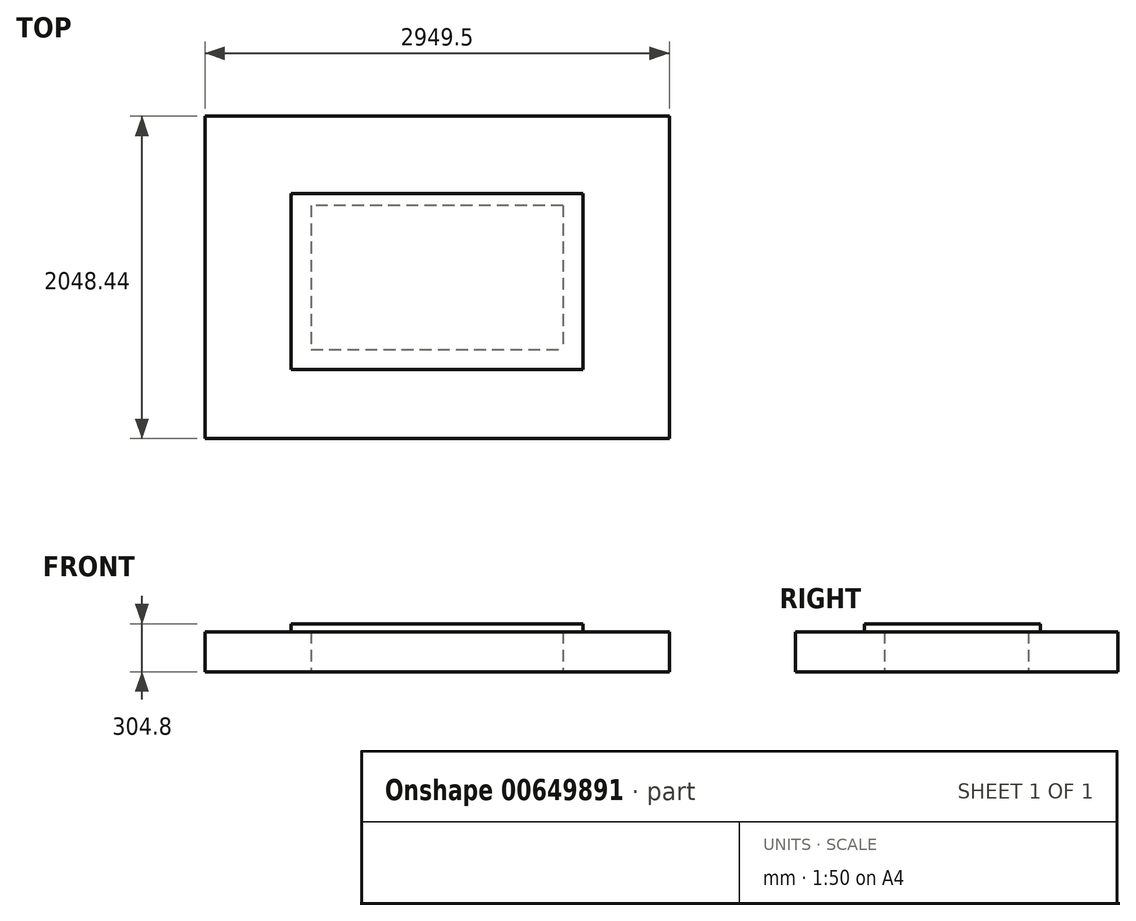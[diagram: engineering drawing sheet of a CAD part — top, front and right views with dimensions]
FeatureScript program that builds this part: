
annotation { "Feature Type Name" : "Feature", "Feature Type Description" : "" }
export const myFeature = defineFeature(function(context is Context, id is Id, definition is map)
    precondition{}
    {
        {
            var Q0;
            Q0=qCreatedBy(makeId("Top.planeOp"),FACE);
            var sketch = newSketch(context, id + "F0", { "sketchPlane" : qUnion([Q0])});
            skLineSegment(sketch, "E0.bottom", {"start": v(800.1, -457.2) * mm, "end": v(-800.1, -457.2) * mm});
            skLineSegment(sketch, "E0.top", {"start": v(800.1, 457.2) * mm, "end": v(-800.1, 457.2) * mm});
            skLineSegment(sketch, "E0.left", {"start": v(800.1, -457.2) * mm, "end": v(800.1, 457.2) * mm});
            skLineSegment(sketch, "E0.right", {"start": v(-800.1, -457.2) * mm, "end": v(-800.1, 457.2) * mm});
            skPoint(sketch, "E0.middle", {"position": v(0, 0) * mm});
            skLineSegment(sketch, "E1.bottom", {"start": v(1474.75, -1024.22) * mm, "end": v(-1474.75, -1024.22) * mm});
            skLineSegment(sketch, "E1.top", {"start": v(1474.75, 1024.22) * mm, "end": v(-1474.75, 1024.22) * mm});
            skLineSegment(sketch, "E1.left", {"start": v(1474.75, -1024.22) * mm, "end": v(1474.75, 1024.22) * mm});
            skLineSegment(sketch, "E1.right", {"start": v(-1474.75, -1024.22) * mm, "end": v(-1474.75, 1024.22) * mm});
            skSolve(sketch);
        }
        {
            var Q0;
            Q0=makeQuery(id+"F0.imprint","IMPRINT",FACE,{"disambiguationData":[TD([[makeQuery(id+"F0.imprint","IMPRINT",EDGE,{"derivedFrom":sQuery(id+"F0.wireOp",EDGE,"E0.bottom")}),1.0]])]});
            extrude(context, id + "F1", {"entities" : qUnion([Q0]), "depth" : 254 * mm, "offsetDistance" : 25.4 * mm});
        }
        {
            var Q0;
            Q0=makeQuery(id+"F1.opExtrude","CAP_FACE",FACE,{"disambiguationData":[OSD([sQuery(id+"F0.wireOp",EDGE,"E0.bottom"),sQuery(id+"F0.wireOp",EDGE,"E0.top"),sQuery(id+"F0.wireOp",EDGE,"E0.left"),sQuery(id+"F0.wireOp",EDGE,"E0.right"),sQuery(id+"F0.wireOp",EDGE,"E1.bottom"),sQuery(id+"F0.wireOp",EDGE,"E1.top"),sQuery(id+"F0.wireOp",EDGE,"E1.left"),sQuery(id+"F0.wireOp",EDGE,"E1.right")])],"isStart":false});
            var sketch = newSketch(context, id + "F2", { "sketchPlane" : qUnion([Q0])});
            skLineSegment(sketch, "E2.bottom", {"start": v(-800.1, -457.2) * mm, "end": v(800.1, -457.2) * mm});
            skLineSegment(sketch, "E2.top", {"start": v(-927.1, -584.2) * mm, "end": v(927.1, -584.2) * mm});
            skLineSegment(sketch, "E2.left", {"start": v(-927.1, -457.2) * mm, "end": v(-927.1, -584.2) * mm});
            skLineSegment(sketch, "E2.right", {"start": v(927.1, -457.2) * mm, "end": v(927.1, -584.2) * mm});
            skLineSegment(sketch, "E3.top", {"start": v(927.1, 533.4) * mm, "end": v(800.1, 533.4) * mm});
            skLineSegment(sketch, "E3.left", {"start": v(927.1, -457.2) * mm, "end": v(927.1, 533.4) * mm});
            skLineSegment(sketch, "E3.right", {"start": v(800.1, -457.2) * mm, "end": v(800.1, 457.2) * mm});
            skLineSegment(sketch, "E4.bottom", {"start": v(800.1, 533.4) * mm, "end": v(-927.1, 533.4) * mm});
            skLineSegment(sketch, "E4.top", {"start": v(800.1, 457.2) * mm, "end": v(-800.1, 457.2) * mm});
            skLineSegment(sketch, "E4.right", {"start": v(-927.1, 533.4) * mm, "end": v(-927.1, 457.2) * mm});
            skLineSegment(sketch, "E5.top", {"start": v(-927.1, 533.4) * mm, "end": v(-800.1, 533.4) * mm});
            skLineSegment(sketch, "E5.left", {"start": v(-927.1, -457.2) * mm, "end": v(-927.1, 533.4) * mm});
            skLineSegment(sketch, "E5.right", {"start": v(-800.1, -457.2) * mm, "end": v(-800.1, 457.2) * mm});
            skLineSegment(sketch, "E6", {"start": v(-800.1, 457.2) * mm, "end": v(-927.1, 533.4) * mm});
            skLineSegment(sketch, "E7", {"start": v(800.1, 457.2) * mm, "end": v(927.1, 533.4) * mm});
            skLineSegment(sketch, "E8", {"start": v(800.1, -457.2) * mm, "end": v(927.1, -584.2) * mm});
            skLineSegment(sketch, "E9", {"start": v(-800.1, -457.2) * mm, "end": v(-927.1, -584.2) * mm});
            skSolve(sketch);
        }
        {
            var Q0;
            {var subQ3=sQuery(id+"F2.wireOp",EDGE,"E2.left");Q0=makeQuery(id+"F2.imprint","IMPRINT",FACE,{"disambiguationData":[TD([[makeQuery(id+"F2.imprint","IMPRINT",EDGE,{"derivedFrom":subQ3}),1.0]])]});}
            var Q1;
            Q1=makeQuery(id+"F2.imprint","IMPRINT",FACE,{"disambiguationData":[TD([[makeQuery(id+"F2.imprint","IMPRINT",EDGE,{"derivedFrom":sQuery(id+"F2.wireOp",EDGE,"E3.top")}),1.0]])]});
            var Q2;
            Q2=makeQuery(id+"F2.imprint","IMPRINT",FACE,{"disambiguationData":[TD([[makeQuery(id+"F2.imprint","IMPRINT",EDGE,{"derivedFrom":sQuery(id+"F2.wireOp",EDGE,"E2.right")}),-1.0]])]});
            var Q3;
            Q3=makeQuery(id+"F2.imprint","IMPRINT",FACE,{"disambiguationData":[TD([[makeQuery(id+"F2.imprint","IMPRINT",EDGE,{"derivedFrom":sQuery(id+"F2.wireOp",EDGE,"E2.bottom")}),1.0]])]});
            extrude(context, id + "F3", {"entities" : qUnion([Q0, Q1, Q2, Q3]), "operationType" : NewBodyOperationType.ADD, "depth" : 50.8 * mm, "offsetDistance" : 25.4 * mm});
        }
        {
            var Q0;
            Q0=makeQuery(id+"F3.boolean.opBoolean","MERGE",FACE,{"derivedFrom":[makeQuery(id+"F1.opExtrude","SWEPT_FACE",FACE,{"disambiguationData":[OSD([sQuery(id+"F0.wireOp",EDGE,"E0.bottom")])]}),makeQuery(id+"F3.opExtrude","SWEPT_FACE",FACE,{"disambiguationData":[OSD([sQuery(id+"F2.wireOp",EDGE,"E2.bottom")])]})]});
            var sketch = newSketch(context, id + "F4", { "sketchPlane" : qUnion([Q0])});
            skLineSegment(sketch, "E10.bottom", {"start": v(800.1, 304.8) * mm, "end": v(-800.1, 304.8) * mm});
            skLineSegment(sketch, "E10.top", {"start": v(800.1, 254) * mm, "end": v(-800.1, 254) * mm});
            skLineSegment(sketch, "E10.left", {"start": v(800.1, 304.8) * mm, "end": v(800.1, 254) * mm});
            skLineSegment(sketch, "E10.right", {"start": v(-800.1, 304.8) * mm, "end": v(-800.1, 254) * mm});
            skSolve(sketch);
        }
        {
            var Q0;
            Q0=makeQuery(id+"F4.imprint","IMPRINT",FACE,{"disambiguationData":[TD([[makeQuery(id+"F4.imprint","IMPRINT",EDGE,{"derivedFrom":sQuery(id+"F4.wireOp",EDGE,"E10.bottom")}),-1.0]])]});
            var Q1;
            Q1=makeQuery(id+"F3.boolean.opBoolean","MERGE",FACE,{"derivedFrom":[makeQuery(id+"F1.opExtrude","SWEPT_FACE",FACE,{"disambiguationData":[OSD([sQuery(id+"F0.wireOp",EDGE,"E0.top")])]}),makeQuery(id+"F3.opExtrude","SWEPT_FACE",FACE,{"disambiguationData":[OSD([sQuery(id+"F2.wireOp",EDGE,"E4.top")])]})]});
            extrude(context, id + "F5", {"entities" : qUnion([Q0]), "operationType" : NewBodyOperationType.ADD, "endBound" : BoundingType.UP_TO_SURFACE, "depth" : 25.4 * mm, "endBoundEntityFace" : qUnion([Q1]), "offsetDistance" : 25.4 * mm});
        }
    });
